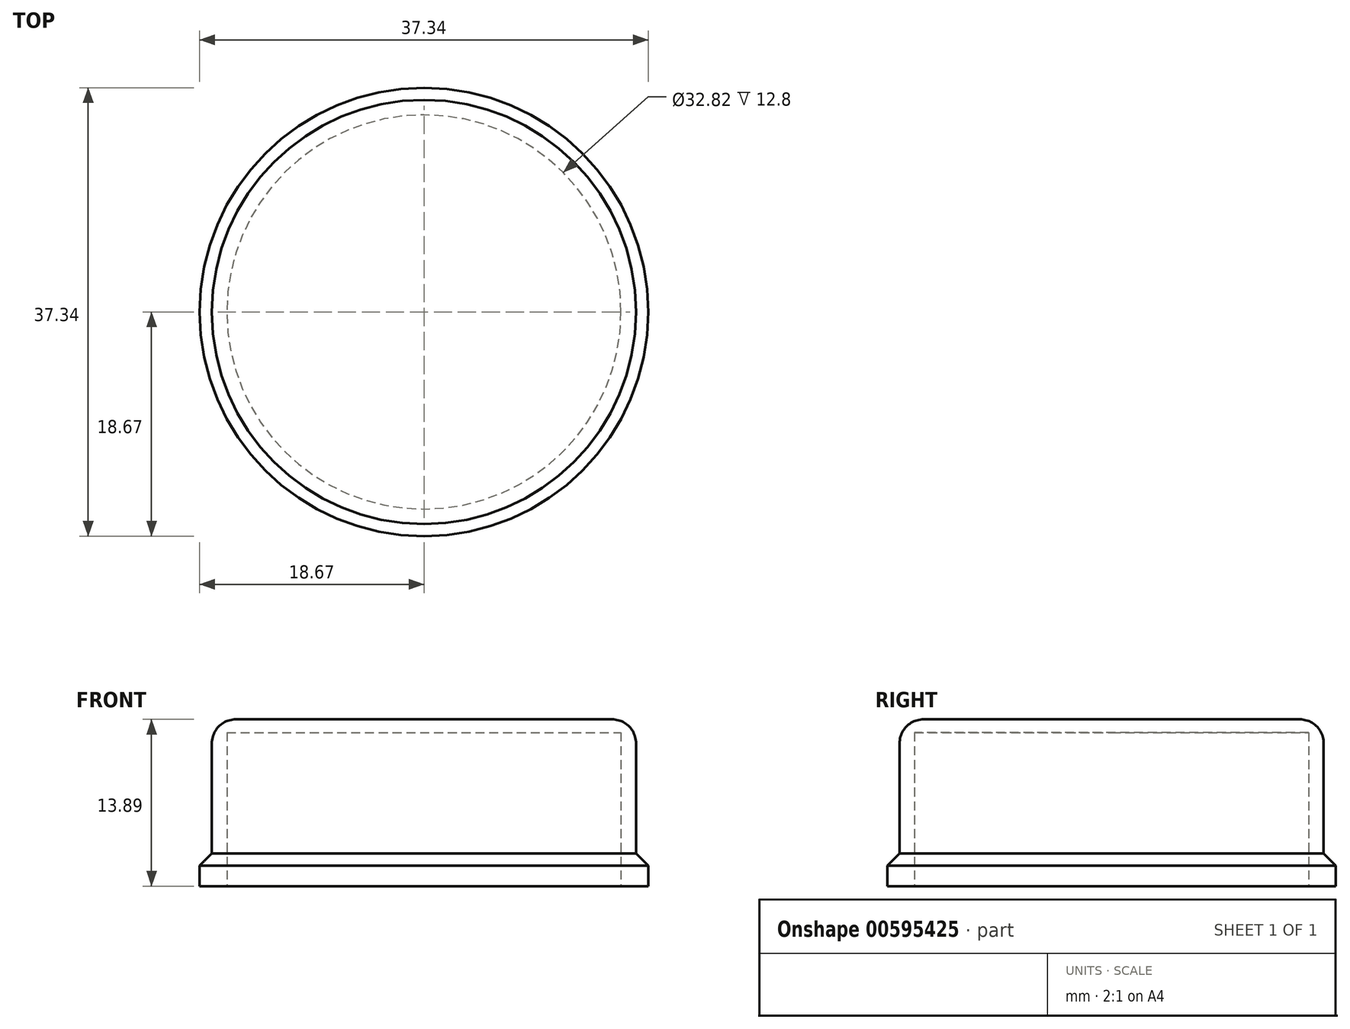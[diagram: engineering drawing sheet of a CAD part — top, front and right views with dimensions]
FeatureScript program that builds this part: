
annotation { "Feature Type Name" : "Feature", "Feature Type Description" : "" }
export const myFeature = defineFeature(function(context is Context, id is Id, definition is map)
    precondition{}
    {
        {
            var Q0;
            Q0=qCreatedBy(makeId("Front.planeOp"),FACE);
            var sketch = newSketch(context, id + "F0", { "sketchPlane" : qUnion([Q0])});
            skLineSegment(sketch, "E0", {"start": v(1.66, 7.98) * mm, "end": v(17.66, 7.98) * mm});
            skLineSegment(sketch, "E1", {"start": v(17.66, 7.98) * mm, "end": v(17.66, -3.18) * mm});
            skLineSegment(sketch, "E2", {"start": v(17.66, -3.18) * mm, "end": v(18.67, -4.2) * mm});
            skLineSegment(sketch, "E3", {"start": v(18.67, -4.2) * mm, "end": v(18.67, -5.91) * mm});
            skLineSegment(sketch, "E4", {"start": v(18.67, -5.91) * mm, "end": v(16.4, -5.91) * mm});
            skLineSegment(sketch, "E5", {"start": v(16.4, -5.91) * mm, "end": v(16.4, 6.89) * mm});
            skLineSegment(sketch, "E6", {"start": v(16.4, 6.89) * mm, "end": v(1.5, 6.89) * mm});
            skLineSegment(sketch, "E7", {"start": v(1.5, 6.89) * mm, "end": v(0, 6.89) * mm});
            skLineSegment(sketch, "E8", {"start": v(0, 6.89) * mm, "end": v(0, 7.98) * mm});
            skLineSegment(sketch, "E9", {"start": v(0, 7.98) * mm, "end": v(1.66, 7.98) * mm});
            skSolve(sketch);
        }
        {
            var Q0;
            Q0=makeQuery(id+"F0.imprint","IMPRINT",FACE,{"disambiguationData":[TD([[makeQuery(id+"F0.imprint","IMPRINT",EDGE,{"derivedFrom":sQuery(id+"F0.wireOp",EDGE,"E0")}),-1.0]])]});
            var Q1;
            Q1=sQuery(id+"F0.wireOp",EDGE,"E8");
            revolve(context, id + "F1", {"entities" : qUnion([Q0]), "axis" : qUnion([Q1]), "revolveType" : RevolveType.FULL});
        }
        {
            var Q0;
            Q0=makeQuery(id+"F1.opRevolve","SWEPT_EDGE",EDGE,{"disambiguationData":[OSD([sQuery(id+"F0.wireOp",EDGE,"E0"),sQuery(id+"F0.wireOp",EDGE,"E1")])]});
            fillet(context, id + "F2", {"entities" : qUnion([Q0]), "radius" : 2 * mm, "tangentPropagation" : true, "allowEdgeOverflow" : false});
        }
    });
